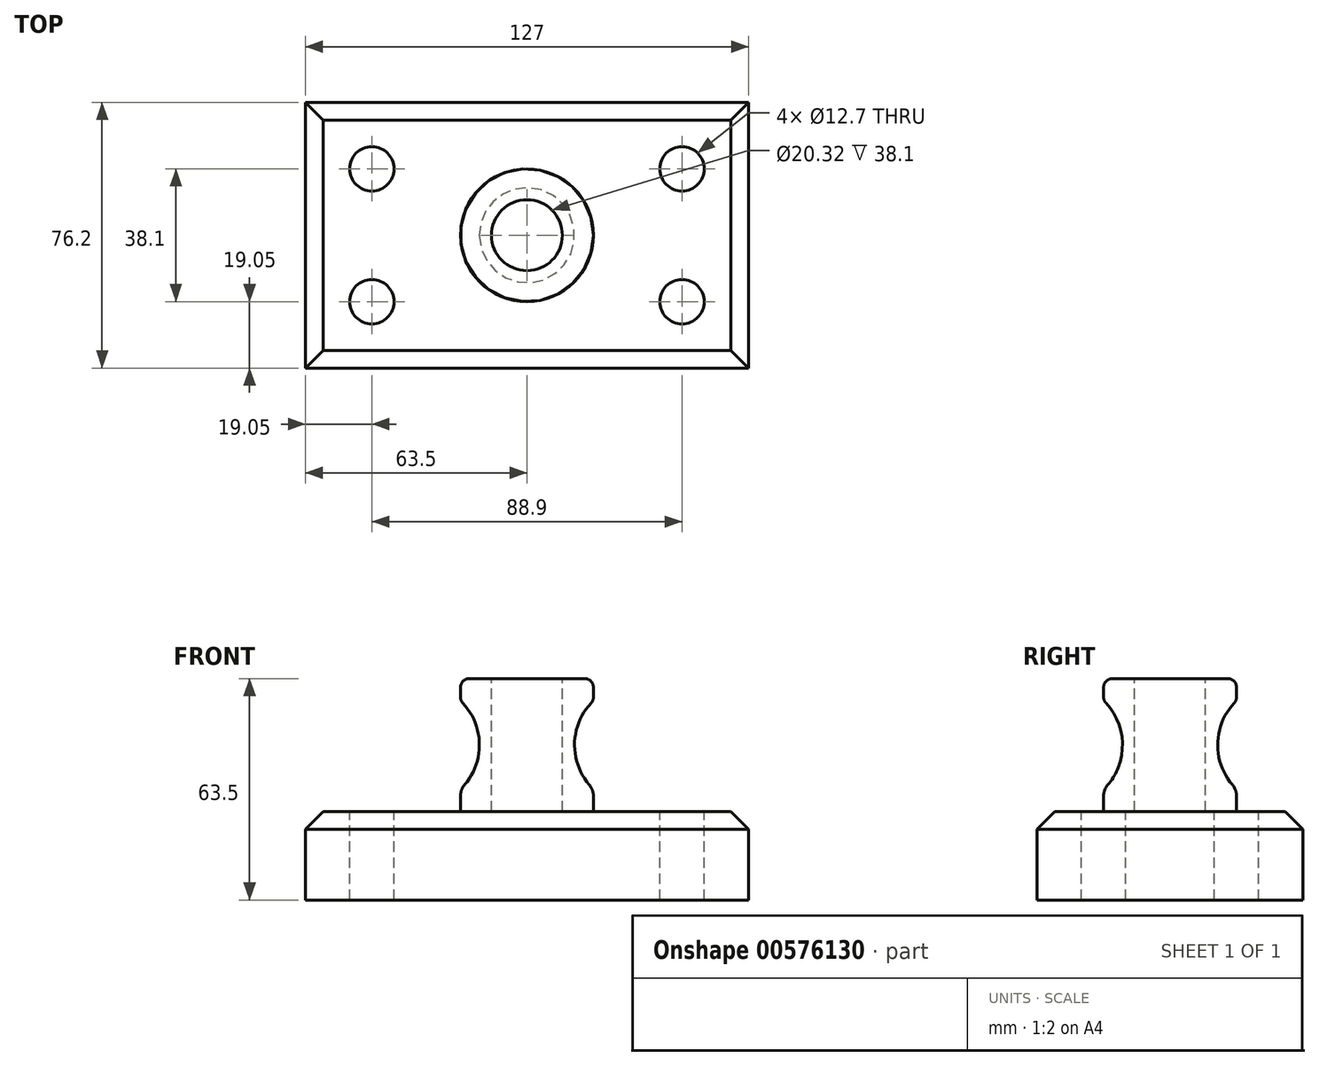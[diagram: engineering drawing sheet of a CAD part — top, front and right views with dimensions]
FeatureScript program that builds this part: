
annotation { "Feature Type Name" : "Feature", "Feature Type Description" : "" }
export const myFeature = defineFeature(function(context is Context, id is Id, definition is map)
    precondition{}
    {
        {
            var Q0;
            Q0=qCreatedBy(makeId("Top.planeOp"),FACE);
            var sketch = newSketch(context, id + "F0", { "sketchPlane" : qUnion([Q0])});
            skLineSegment(sketch, "E0.bottom", {"start": v(-63.5, 38.1) * mm, "end": v(63.5, 38.1) * mm});
            skLineSegment(sketch, "E0.top", {"start": v(-63.5, -38.1) * mm, "end": v(63.5, -38.1) * mm});
            skLineSegment(sketch, "E0.left", {"start": v(-63.5, 38.1) * mm, "end": v(-63.5, -38.1) * mm});
            skLineSegment(sketch, "E0.right", {"start": v(63.5, 38.1) * mm, "end": v(63.5, -38.1) * mm});
            skPoint(sketch, "E0.middle", {"position": v(0, 0) * mm});
            skSolve(sketch);
        }
        {
            var Q0;
            Q0=makeQuery(id+"F0.imprint","IMPRINT",FACE,{"disambiguationData":[TD([[makeQuery(id+"F0.imprint","IMPRINT",EDGE,{"derivedFrom":sQuery(id+"F0.wireOp",EDGE,"E0.bottom")}),-1.0]])]});
            extrude(context, id + "F1", {"entities" : qUnion([Q0]), "depth" : 25.4 * mm, "offsetDistance" : 25.4 * mm});
        }
        {
            var Q0;
            Q0=makeQuery(id+"F1.opExtrude","CAP_FACE",FACE,{"disambiguationData":[OSD([sQuery(id+"F0.wireOp",EDGE,"E0.bottom"),sQuery(id+"F0.wireOp",EDGE,"E0.top"),sQuery(id+"F0.wireOp",EDGE,"E0.left"),sQuery(id+"F0.wireOp",EDGE,"E0.right")])],"isStart":false});
            var sketch = newSketch(context, id + "F2", { "sketchPlane" : qUnion([Q0])});
            skCircle(sketch, "E1", {"center": v(-44.45, 19.05) * mm, "radius": 6.35 * mm});
            skCircle(sketch, "E2", {"center": v(-44.45, -19.05) * mm, "radius": 6.35 * mm});
            skCircle(sketch, "E3", {"center": v(44.45, 19.05) * mm, "radius": 6.35 * mm});
            skCircle(sketch, "E4", {"center": v(44.45, -19.05) * mm, "radius": 6.35 * mm});
            skSolve(sketch);
        }
        {
            var Q0;
            Q0=makeQuery(id+"F2.imprint","IMPRINT",FACE,{"disambiguationData":[TD([[makeQuery(id+"F2.imprint","IMPRINT",EDGE,{"derivedFrom":sQuery(id+"F2.wireOp",EDGE,"E2")}),1.0]])]});
            var Q1;
            Q1=makeQuery(id+"F2.imprint","IMPRINT",FACE,{"disambiguationData":[TD([[makeQuery(id+"F2.imprint","IMPRINT",EDGE,{"derivedFrom":sQuery(id+"F2.wireOp",EDGE,"E4")}),1.0]])]});
            var Q2;
            Q2=makeQuery(id+"F2.imprint","IMPRINT",FACE,{"disambiguationData":[TD([[makeQuery(id+"F2.imprint","IMPRINT",EDGE,{"derivedFrom":sQuery(id+"F2.wireOp",EDGE,"E3")}),1.0]])]});
            var Q3;
            Q3=makeQuery(id+"F2.imprint","IMPRINT",FACE,{"disambiguationData":[TD([[makeQuery(id+"F2.imprint","IMPRINT",EDGE,{"derivedFrom":sQuery(id+"F2.wireOp",EDGE,"E1")}),1.0]])]});
            extrude(context, id + "F3", {"entities" : qUnion([Q0, Q1, Q2, Q3]), "operationType" : NewBodyOperationType.REMOVE, "oppositeDirection" : true, "depth" : 25.4 * mm, "offsetDistance" : 25.4 * mm});
        }
        {
            var Q0;
            Q0=makeQuery(id+"F1.opExtrude","CAP_EDGE",EDGE,{"disambiguationData":[OSD([sQuery(id+"F0.wireOp",EDGE,"E0.top")])],"isStart":false});
            var Q1;
            Q1=makeQuery(id+"F1.opExtrude","CAP_EDGE",EDGE,{"disambiguationData":[OSD([sQuery(id+"F0.wireOp",EDGE,"E0.left")])],"isStart":false});
            var Q2;
            Q2=makeQuery(id+"F1.opExtrude","CAP_EDGE",EDGE,{"disambiguationData":[OSD([sQuery(id+"F0.wireOp",EDGE,"E0.bottom")])],"isStart":false});
            var Q3;
            Q3=makeQuery(id+"F1.opExtrude","CAP_EDGE",EDGE,{"disambiguationData":[OSD([sQuery(id+"F0.wireOp",EDGE,"E0.right")])],"isStart":false});
            chamfer(context, id + "F4", {"entities" : qUnion([Q0, Q1, Q2, Q3]), "width" : 5.08 * mm, "tangentPropagation" : true});
        }
        {
            var Q0;
            Q0=makeQuery(id+"F1.opExtrude","CAP_FACE",FACE,{"disambiguationData":[OSD([sQuery(id+"F0.wireOp",EDGE,"E0.bottom"),sQuery(id+"F0.wireOp",EDGE,"E0.top"),sQuery(id+"F0.wireOp",EDGE,"E0.left"),sQuery(id+"F0.wireOp",EDGE,"E0.right")])],"isStart":false});
            var sketch = newSketch(context, id + "F5", { "sketchPlane" : qUnion([Q0])});
            skCircle(sketch, "E5", {"center": v(0, 0) * mm, "radius": 19.05 * mm});
            skSolve(sketch);
        }
        {
            var Q0;
            Q0=makeQuery(id+"F5.imprint","IMPRINT",FACE,{"disambiguationData":[TD([[makeQuery(id+"F5.imprint","IMPRINT",EDGE,{"derivedFrom":sQuery(id+"F5.wireOp",EDGE,"E5")}),1.0]])]});
            extrude(context, id + "F6", {"entities" : qUnion([Q0]), "operationType" : NewBodyOperationType.ADD, "depth" : 6.35 * mm, "offsetDistance" : 25.4 * mm});
        }
        {
            var Q0;
            Q0=qCreatedBy(makeId("Front.planeOp"),FACE);
            var sketch = newSketch(context, id + "F7", { "sketchPlane" : qUnion([Q0])});
            skLineSegment(sketch, "E6", {"start": v(0, 31.75) * mm, "end": v(0, 57.15) * mm});
            skLineSegment(sketch, "E7", {"start": v(0, 57.15) * mm, "end": v(19.05, 57.15) * mm});
            skLineSegment(sketch, "E8", {"start": v(0, 31.75) * mm, "end": v(19.05, 31.75) * mm});
            skArc(sketch, "E9", {"start": v(19.05, 57.15) * mm, "mid": v(13.64, 44.45) * mm, "end": v(19.05, 31.75) * mm});
            skSolve(sketch);
        }
        {
            var Q0;
            Q0=makeQuery(id+"F7.imprint","IMPRINT",FACE,{"disambiguationData":[TD([[makeQuery(id+"F7.imprint","IMPRINT",EDGE,{"derivedFrom":sQuery(id+"F7.wireOp",EDGE,"E6")}),-1.0]])]});
            var Q1;
            Q1=sQuery(id+"F7.wireOp",EDGE,"E6");
            revolve(context, id + "F8", {"operationType" : NewBodyOperationType.ADD, "entities" : qUnion([Q0]), "axis" : qUnion([Q1]), "revolveType" : RevolveType.FULL});
        }
        {
            var Q0;
            Q0=makeQuery(id+"F8.opRevolve","SWEPT_FACE",FACE,{"disambiguationData":[OSD([sQuery(id+"F7.wireOp",EDGE,"E7")])]});
            var sketch = newSketch(context, id + "F9", { "sketchPlane" : qUnion([Q0])});
            skCircle(sketch, "E10", {"center": v(0, 0) * mm, "radius": 19.05 * mm});
            skSolve(sketch);
        }
        {
            var Q0;
            Q0=makeQuery(id+"F9.imprint","IMPRINT",FACE,{"disambiguationData":[TD([[makeQuery(id+"F9.imprint","IMPRINT",EDGE,{"derivedFrom":sQuery(id+"F9.wireOp",EDGE,"E10")}),-1.0]])]});
            extrude(context, id + "F10", {"entities" : qUnion([Q0]), "operationType" : NewBodyOperationType.ADD, "depth" : 6.35 * mm, "offsetDistance" : 25.4 * mm});
        }
        {
            var Q0;
            Q0=makeQuery(id+"F10.opExtrude","CAP_FACE",FACE,{"disambiguationData":[OSD([sQuery(id+"F9.wireOp",EDGE,"E10")])],"isStart":false});
            var sketch = newSketch(context, id + "F11", { "sketchPlane" : qUnion([Q0])});
            skCircle(sketch, "E11", {"center": v(0, 0) * mm, "radius": 10.16 * mm});
            skSolve(sketch);
        }
        {
            var Q0;
            Q0 = qSketchRegion(id + "F11", true);
            extrude(context, id + "F12", {"entities" : qUnion([Q0]), "operationType" : NewBodyOperationType.REMOVE, "oppositeDirection" : true, "depth" : 38.1 * mm, "offsetDistance" : 25.4 * mm});
        }
        {
            var Q0;
            Q0=makeQuery(id+"F10.opExtrude","CAP_EDGE",EDGE,{"disambiguationData":[OSD([sQuery(id+"F9.wireOp",EDGE,"E10")])],"isStart":false});
            var Q1;
            Q1=makeQuery(id+"F10.boolean.opBoolean","MERGE",EDGE,{"derivedFrom":[makeQuery(id+"F8.opRevolve","SWEPT_EDGE",EDGE,{"disambiguationData":[OSD([sQuery(id+"F7.wireOp",EDGE,"E7"),sQuery(id+"F7.wireOp",EDGE,"E9")])]}),makeQuery(id+"F10.opExtrude","CAP_EDGE",EDGE,{"disambiguationData":[OSD([sQuery(id+"F9.wireOp",EDGE,"E10")])],"isStart":true})]});
            fillet(context, id + "F13", {"entities" : qUnion([Q0, Q1]), "radius" : 2.54 * mm, "tangentPropagation" : true, "allowEdgeOverflow" : false});
        }
        {
            var Q0;
            Q0=makeQuery(id+"F8.boolean.opBoolean","MERGE",EDGE,{"derivedFrom":[makeQuery(id+"F6.opExtrude","CAP_EDGE",EDGE,{"disambiguationData":[OSD([sQuery(id+"F5.wireOp",EDGE,"E5")])],"isStart":false}),makeQuery(id+"F8.opRevolve","SWEPT_EDGE",EDGE,{"disambiguationData":[OSD([sQuery(id+"F7.wireOp",EDGE,"E8"),sQuery(id+"F7.wireOp",EDGE,"E9")])]})]});
            fillet(context, id + "F14", {"entities" : qUnion([Q0]), "radius" : 5.08 * mm, "tangentPropagation" : true, "rho" : 0.5, "crossSection" : FilletCrossSection.CONIC, "allowEdgeOverflow" : false});
        }
    });
